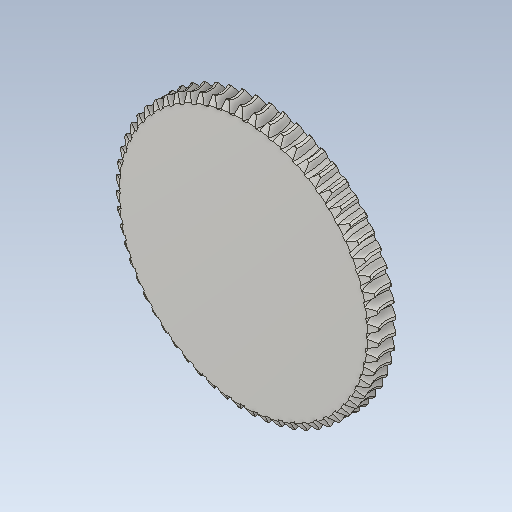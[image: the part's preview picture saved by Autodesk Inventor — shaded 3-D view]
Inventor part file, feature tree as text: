
AUTODESK INVENTOR PART (.ipt)
format: ipt  version: 2021 (Build 250183000, 183)  size: 1,139,712 bytes
history: native  units: mm (DEFAULTED — no unit token found)
features: other x8, plane x3, pattern_circular x1, sketch x1
ambient origin geometry x5: Origin, X Axis, Y Axis, Z Axis, Center Point
bodies: Solid1 (feature_tree)
feature tree (13):
  other  "Tooth Plane"
  other  "Base Body Sketch"
  other  "Base Body"
  other  "Base Body2"
  plane  "Work Plane13"
  other  "Tooth"
  pattern_circular  "Tooth Pattern"  [2 undecoded]
  plane  "Work Plane14"
  plane  "Work Plane15"
  other  "Tooth Sketch"
  sketch  "Sketch8"  dims[d35=90.0deg d37=-0.996687mm d38=70.744372mm d39=3.490659mm d40=7.680818mm d41=10.106339mm d42=1.905mm d43=90.0deg d44=600.0mm d46=360.0deg d50=5.318254mm d68=70.744372mm d69=0.0mm d73=0.0mm d75=0.523599mm d77=121.276067mm d78=12.3mm d79=0.0mm d80=0.0mm d81=0.0mm d82=0.0mm d83=0.523599mm d84=0.0mm d85=180.0deg d86=70.744372mm d87=127.33987mm d89=16.170142mm d90=90.0deg d92=12.3mm d93=70.744372mm]
  other  "Srf1"
  other  "Pitch Diameter"
note: 2 required parameter values undecoded (feature->parameter linkage not recoverable at this tier; creation-order binding heuristic only, values carry confidence <= 0.55)
